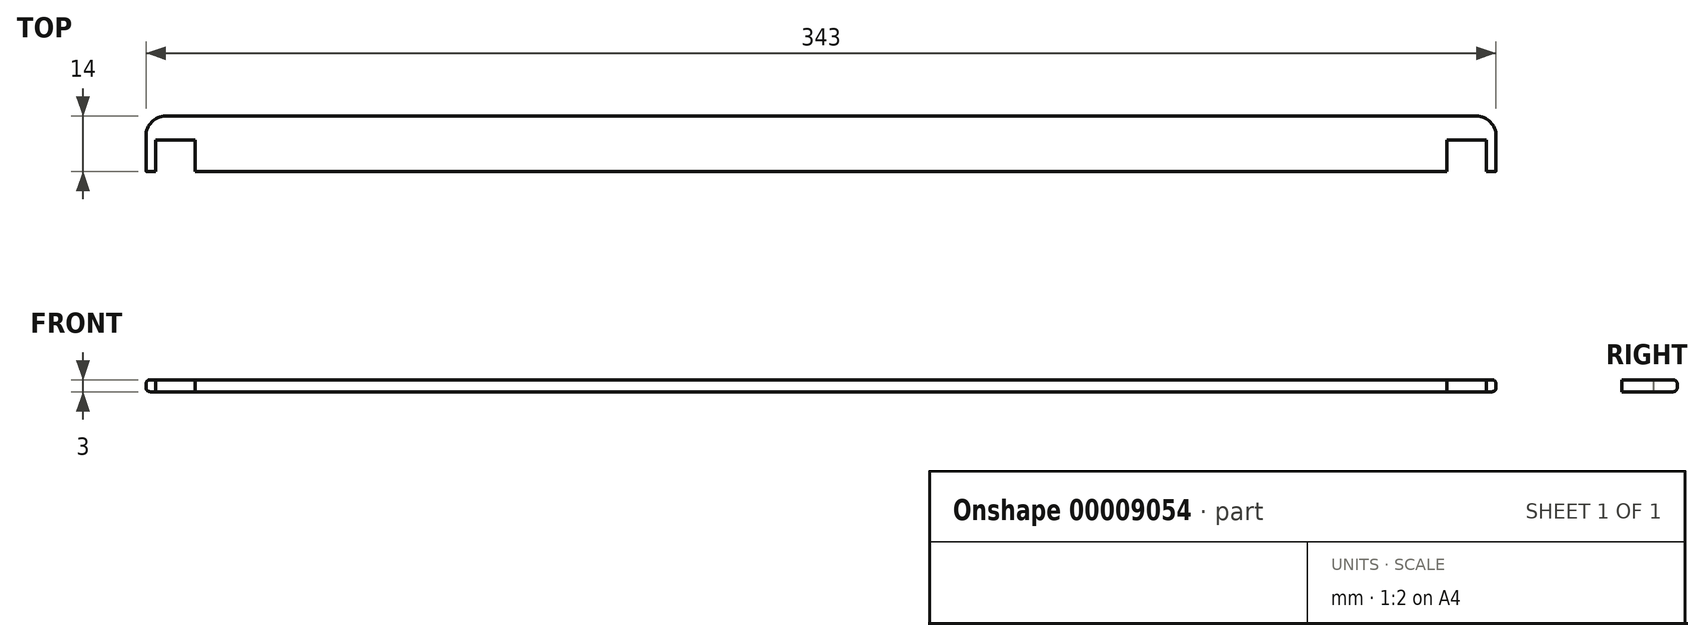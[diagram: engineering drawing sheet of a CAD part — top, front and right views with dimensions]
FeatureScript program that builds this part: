
annotation { "Feature Type Name" : "Feature", "Feature Type Description" : "" }
export const myFeature = defineFeature(function(context is Context, id is Id, definition is map)
    precondition{}
    {
        {
            var Q0;
            Q0=qCreatedBy(makeId("Top.planeOp"),FACE);
            var sketch = newSketch(context, id + "F0", { "sketchPlane" : qUnion([Q0])});
            skLineSegment(sketch, "E0", {"start": v(0, 0) * mm, "end": v(159, 0) * mm});
            skLineSegment(sketch, "E1", {"start": v(159, 0) * mm, "end": v(159, 8) * mm});
            skLineSegment(sketch, "E2", {"start": v(159, 8) * mm, "end": v(169, 8) * mm});
            skLineSegment(sketch, "E3", {"start": v(169, 8) * mm, "end": v(169, 0) * mm});
            skLineSegment(sketch, "E4", {"start": v(169, 0) * mm, "end": v(171.5, 0) * mm});
            skLineSegment(sketch, "E5", {"start": v(171.5, 0) * mm, "end": v(171.5, 14) * mm});
            skLineSegment(sketch, "E6", {"start": v(171.5, 14) * mm, "end": v(0, 14) * mm});
            skLineSegment(sketch, "E7.0.MirrorCS", {"start": v(-171.5, 14) * mm, "end": v(0, 14) * mm});
            skLineSegment(sketch, "E8.0.MirrorCS", {"start": v(-171.5, 0) * mm, "end": v(-171.5, 14) * mm});
            skLineSegment(sketch, "E9.0.MirrorCS", {"start": v(-169, 0) * mm, "end": v(-171.5, 0) * mm});
            skLineSegment(sketch, "E10.0.MirrorCS", {"start": v(-169, 8) * mm, "end": v(-169, 0) * mm});
            skLineSegment(sketch, "E11.0.MirrorCS", {"start": v(-159, 8) * mm, "end": v(-169, 8) * mm});
            skLineSegment(sketch, "E12.0.MirrorCS", {"start": v(-159, 0) * mm, "end": v(-159, 8) * mm});
            skLineSegment(sketch, "E13.0.MirrorCS", {"start": v(0, 0) * mm, "end": v(-159, 0) * mm});
            skSolve(sketch);
        }
        {
            var Q0;
            Q0 = qSketchRegion(id + "F0", true);
            extrude(context, id + "F1", {"entities" : qUnion([Q0]), "depth" : 3 * mm});
        }
        {
            var Q0;
            Q0=makeQuery(id+"F1.opExtrude","SWEPT_EDGE",EDGE,{"disambiguationData":[OSD([sQuery(id+"F0.wireOp",EDGE,"E7.0.MirrorCS"),sQuery(id+"F0.wireOp",EDGE,"E8.0.MirrorCS")])]});
            var Q1;
            Q1=makeQuery(id+"F1.opExtrude","SWEPT_EDGE",EDGE,{"disambiguationData":[OSD([sQuery(id+"F0.wireOp",EDGE,"E5"),sQuery(id+"F0.wireOp",EDGE,"E6")])]});
            fillet(context, id + "F2", {"entities" : qUnion([Q0, Q1]), "radius" : 5 * mm, "tangentPropagation" : true, "allowEdgeOverflow" : false});
        }
        {
            var Q0;
            Q0=makeQuery(id+"F1.opExtrude","CAP_EDGE",EDGE,{"disambiguationData":[OSD([sQuery(id+"F0.wireOp",EDGE,"E5")])],"isStart":true});
            var Q1;
            Q1=makeQuery(id+"F1.opExtrude","CAP_EDGE",EDGE,{"disambiguationData":[OSD([sQuery(id+"F0.wireOp",EDGE,"E5")])],"isStart":false});
            fillet(context, id + "F3", {"entities" : qUnion([Q0, Q1]), "radius" : 1 * mm, "tangentPropagation" : true, "allowEdgeOverflow" : false});
        }
    });
